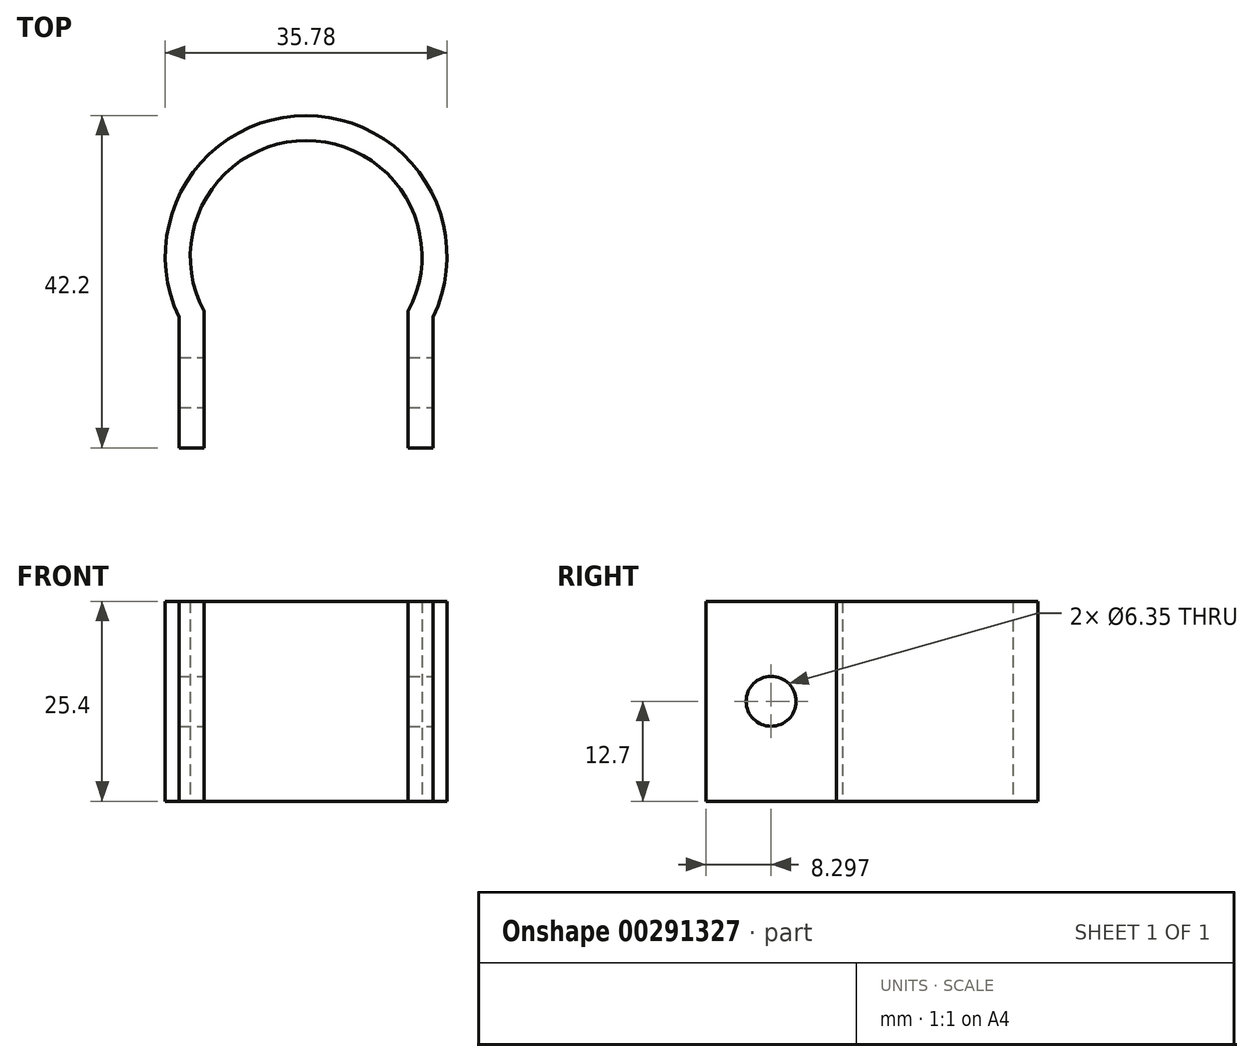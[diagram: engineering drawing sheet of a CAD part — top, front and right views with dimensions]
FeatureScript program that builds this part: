
annotation { "Feature Type Name" : "Feature", "Feature Type Description" : "" }
export const myFeature = defineFeature(function(context is Context, id is Id, definition is map)
    precondition{}
    {
        {
            var Q0;
            Q0=qCreatedBy(makeId("Top.planeOp"),FACE);
            var sketch = newSketch(context, id + "F0", { "sketchPlane" : qUnion([Q0])});
            skArc(sketch, "E0", {"start": v(12.97, -6.96) * mm, "mid": v(0, 14.72) * mm, "end": v(-12.97, -6.96) * mm});
            skLineSegment(sketch, "E1", {"start": v(-12.97, -6.96) * mm, "end": v(-12.97, -24.3) * mm});
            skLineSegment(sketch, "E2", {"start": v(12.97, -6.96) * mm, "end": v(12.97, -24.3) * mm});
            skLineSegment(sketch, "E3.0", {"start": v(-16.14, -7.72) * mm, "end": v(-16.14, -24.3) * mm});
            skArc(sketch, "E3.1", {"start": v(16.14, -7.72) * mm, "mid": v(0, 17.9) * mm, "end": v(-16.14, -7.72) * mm});
            skLineSegment(sketch, "E3.2", {"start": v(16.14, -7.72) * mm, "end": v(16.14, -24.3) * mm});
            skLineSegment(sketch, "E4", {"start": v(-16.14, -24.3) * mm, "end": v(-12.97, -24.3) * mm});
            skLineSegment(sketch, "E5", {"start": v(12.97, -24.3) * mm, "end": v(16.14, -24.3) * mm});
            skSolve(sketch);
        }
        {
            var Q0;
            Q0 = qSketchRegion(id + "F0", true);
            extrude(context, id + "F1", {"entities" : qUnion([Q0]), "depth" : 25.4 * mm});
        }
        {
            var Q0;
            Q0=makeQuery(id+"F1.opExtrude","SWEPT_FACE",FACE,{"disambiguationData":[OSD([sQuery(id+"F0.wireOp",EDGE,"E3.2")])]});
            var sketch = newSketch(context, id + "F2", { "sketchPlane" : qUnion([Q0])});
            skCircle(sketch, "E6", {"center": v(-16.01, 12.7) * mm, "radius": 3.18 * mm});
            skLineSegment(sketch, "E7", {"start": v(-7.72, 25.4) * mm, "end": v(-24.3, 0) * mm});
            skSolve(sketch);
        }
        {
            var Q0;
            Q0=makeQuery(id+"F2.imprint","IMPRINT",FACE,{"disambiguationData":[TD([[makeQuery(id+"F2.imprint","IMPRINT",EDGE,{"derivedFrom":sQuery(id+"F2.wireOp",EDGE,"E6")}),1.0]])]});
            extrude(context, id + "F3", {"entities" : qUnion([Q0]), "operationType" : NewBodyOperationType.REMOVE, "oppositeDirection" : true, "depth" : 63.5 * mm});
        }
    });
